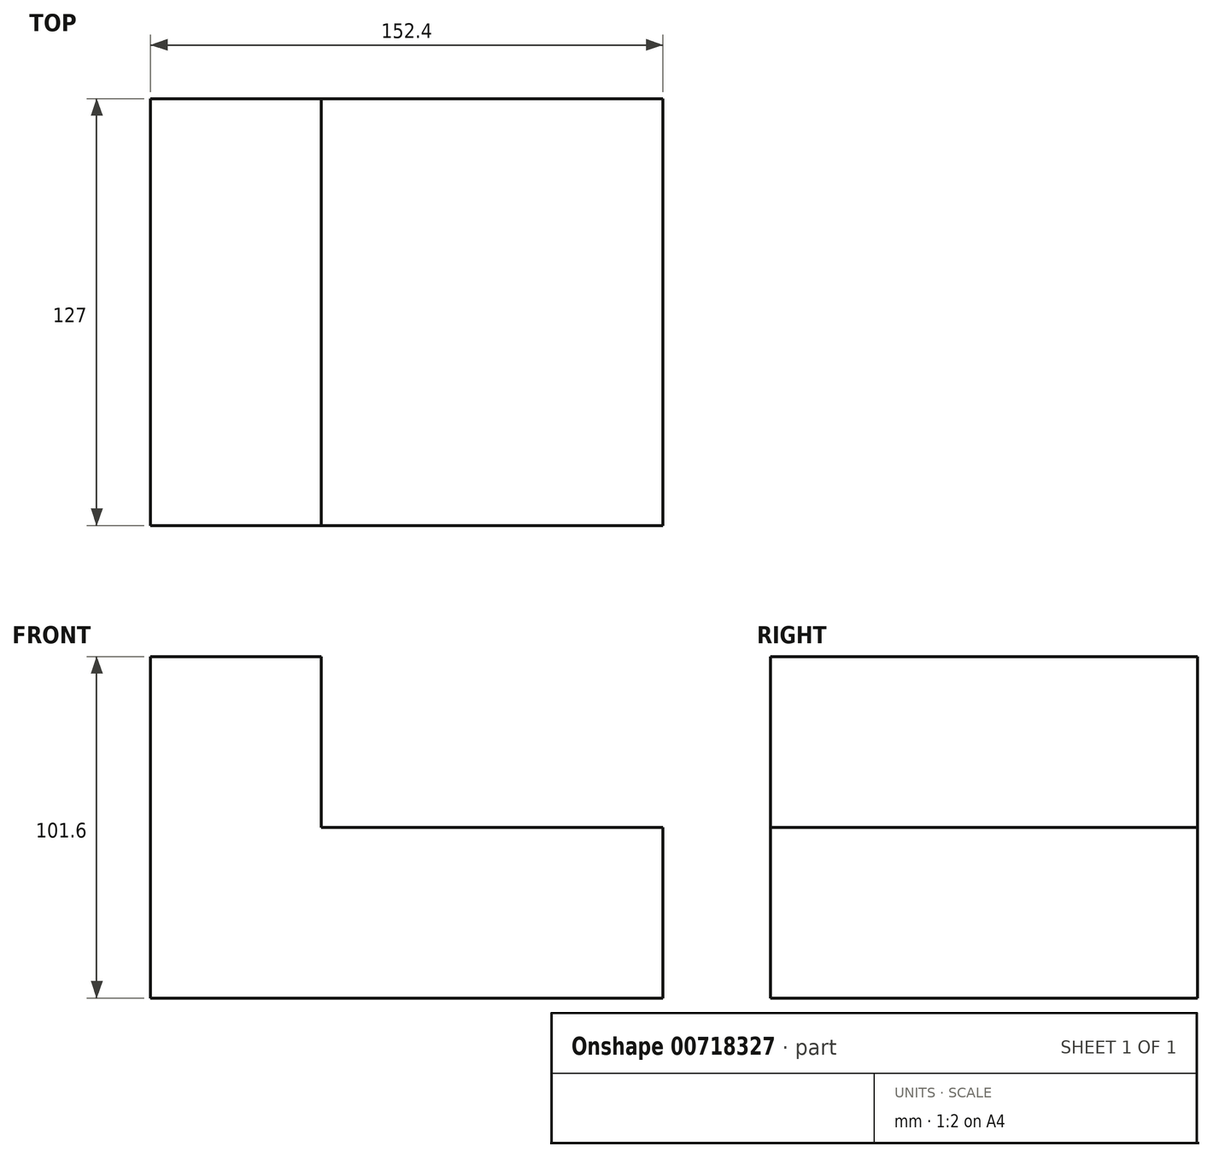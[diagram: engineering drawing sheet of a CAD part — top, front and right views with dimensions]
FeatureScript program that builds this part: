
annotation { "Feature Type Name" : "Feature", "Feature Type Description" : "" }
export const myFeature = defineFeature(function(context is Context, id is Id, definition is map)
    precondition{}
    {
        {
            var Q0;
            Q0=qCreatedBy(makeId("Front.planeOp"),FACE);
            var sketch = newSketch(context, id + "F0", { "sketchPlane" : qUnion([Q0])});
            skLineSegment(sketch, "E0", {"start": v(-50.8, -57.67) * mm, "end": v(101.6, -57.67) * mm});
            skLineSegment(sketch, "E1", {"start": v(101.6, -57.67) * mm, "end": v(101.6, -6.87) * mm});
            skLineSegment(sketch, "E2", {"start": v(101.6, -6.87) * mm, "end": v(0, -6.87) * mm});
            skLineSegment(sketch, "E3", {"start": v(0, -6.87) * mm, "end": v(0, 43.93) * mm});
            skLineSegment(sketch, "E4", {"start": v(0, 43.93) * mm, "end": v(-50.8, 43.93) * mm});
            skLineSegment(sketch, "E5", {"start": v(-50.8, 43.93) * mm, "end": v(-50.8, -57.67) * mm});
            skSolve(sketch);
        }
        {
            var Q0;
            Q0=makeQuery(id+"F0.imprint","IMPRINT",FACE,{"disambiguationData":[TD([[makeQuery(id+"F0.imprint","IMPRINT",EDGE,{"derivedFrom":sQuery(id+"F0.wireOp",EDGE,"E0")}),1.0]])]});
            extrude(context, id + "F1", {"entities" : qUnion([Q0]), "depth" : 127 * mm, "offsetDistance" : 25.4 * mm});
        }
    });
